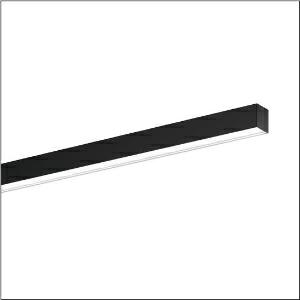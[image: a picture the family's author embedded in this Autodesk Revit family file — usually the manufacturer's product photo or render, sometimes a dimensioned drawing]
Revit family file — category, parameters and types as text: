
# Revit family: silica_21_51mx20db42bb
name_source: partatom
category: Lighting Fixtures
units: mm (PartAtom-declared; Revit-internal decimal feet)

## family parameters
Cut with Voids When Loaded = No
Host = Face
Light Source = No
Part Type = Normal
Room Calculation Point = No
Round Connector Dimension = Use Diameter
Shared = No

## types (1)
- --- (1 x LED, 3000 lm, 19 W, 4000K)
    Apparent Load = 19 VA
    CIE Flux Codes = 48 79 96 100 100
    Color Rendering = 80
    Color Temperature = 4000K
    Default Elevation = 1800 mm
    Description = Silica 21, office luminaire, primary optical cover: cover, of PMMA, opal, light emission: direct distribution, primary light characteristic: symmetric, installation type: surface-mounted, LED, rated luminous flux: 3.000lm, luminous efficacy: 158lm/W, light colour: 840, colour temperature: 4000K, control gear: DALI 2, with terminal, 3+2-pole, max. 2.5mm², mains connection: 220..240V, AC, 50/60Hz, rated input power: 19W, luminaire housing, of aluminium, matt jet black (RAL 9005), length: 1.504mm, width: 53mm, height: 53mm, protection rating (complete): IP20, insulation class (complete): insulation class I (protective earthing), certification: CE, permissible operating ambient temperature: 0..+35°C, standard: EN 50419, packaging unit: 1 piece
    Height = 53 mm
    Lamp = 1 x LED
    Lamp Light Flux = 3000 lm
    Lamp Power = 19 W
    Lamp count = 1
    Length = 1504 mm
    Luminous efficacy = 158 lm/W
    Manufacturer = Siteco
    ModVariant = No
    Model = 51MX20DB42BB
    Mounting Place = Ceiling
    Mounting Type = Surface mounted
    Number of Poles = 1
    OnlyDefault = Yes
    Power Factor = 1
    Product Name = Silica 21
    Product group = office luminaire | ceiling mounted
    ProductGroupID = 301
    Protection Class = Protection class I
    Protection Degree = IP 20
    RLX_Detail_Level = 1
    RLX_Emergency_Light_Flux = 0 lm
    RLX_Emergency_Type = 0
    RLX_Emergency_Type_DB = No
    RlxData = <blob elided: 28749 chars, md5=c4c07f68>
    Socket = socket
    Standby Power = 0 W
    System Light Flux = 3000 lm
    System Power = 19 W
    Type Comments = factory setting: luminous flux: 100 % | dim-lin: 254 | 218 mA
    Type Image = l_1335925.jpg
    URL = http://relux.com
    VarID = @adj_119813
    Voltage = 0 V
    Weight = 0.00 kg
    Width = 53 mm

## geometry (parser evidence)
native form markers: Blend x4, Sweep x11
no freeform markers — native parametric forms only
